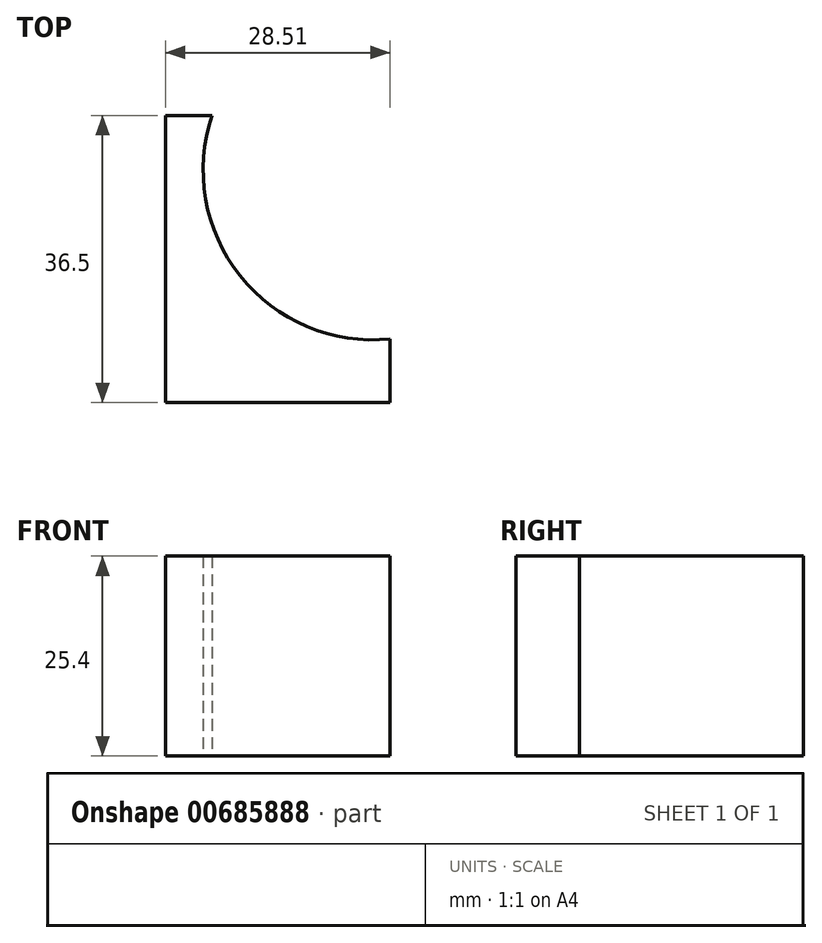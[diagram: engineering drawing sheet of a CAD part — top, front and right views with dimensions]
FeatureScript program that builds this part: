
annotation { "Feature Type Name" : "Feature", "Feature Type Description" : "" }
export const myFeature = defineFeature(function(context is Context, id is Id, definition is map)
    precondition{}
    {
        {
            var Q0;
            Q0=qCreatedBy(makeId("Top.planeOp"),FACE);
            var sketch = newSketch(context, id + "F0", { "sketchPlane" : qUnion([Q0])});
            skLineSegment(sketch, "E0", {"start": v(0, 0) * mm, "end": v(-28.51, 0) * mm});
            skLineSegment(sketch, "E1", {"start": v(-28.51, 0) * mm, "end": v(-28.51, 36.5) * mm});
            skLineSegment(sketch, "E2", {"start": v(-28.51, 36.5) * mm, "end": v(-22.6, 36.5) * mm});
            skLineSegment(sketch, "E3", {"start": v(0, 0) * mm, "end": v(0, 8.09) * mm});
            skArc(sketch, "E4", {"start": v(-22.6, 36.5) * mm, "mid": v(-19.06, 16.13) * mm, "end": v(0, 8.09) * mm});
            skSolve(sketch);
        }
        {
            var Q0;
            Q0 = qSketchRegion(id + "F0", true);
            extrude(context, id + "F1", {"entities" : qUnion([Q0]), "depth" : 25.4 * mm, "offsetDistance" : 25.4 * mm});
        }
    });
